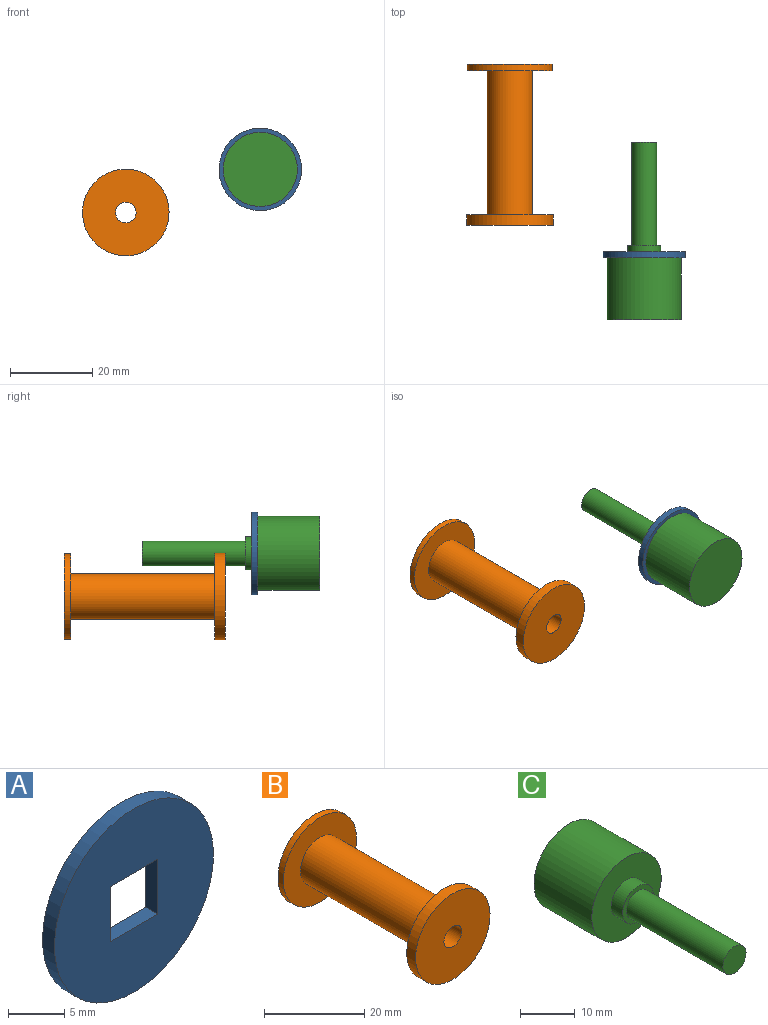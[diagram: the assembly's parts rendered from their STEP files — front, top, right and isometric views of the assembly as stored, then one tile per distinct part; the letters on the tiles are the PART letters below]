
ASSEMBLY  parts=3 mates=1
PART A: 7 faces, bbox 20x1.5x20 mm
  f0: plane 6x1.5mm, normal (0,0,-1), area 9mm2, adj f1,f4,f5,f6
  f1: plane 6x1.5mm, normal (-1,0,0), area 9mm2, adj f0,f2,f5,f6
  f2: plane 6x1.5mm, normal (0,0,1), area 9mm2, adj f1,f4,f5,f6
  f3: cylinder r=10mm len=20mm, axis (0,1,0), area 94.2mm2, adj f5,f6
  f4: plane 6x1.5mm, normal (1,0,0), area 9mm2, adj f0,f2,f5,f6
  f5: plane 20x20mm, normal (0,-1,0), area 278.2mm2, adj f0,f1,f2,f3,f4
  f6: plane 20x20mm, normal (0,1,0), area 278.2mm2, adj f0,f1,f2,f3,f4
PART B: 8 faces, bbox 21x39x21 mm
  f0: cylinder r=10.35mm len=20.7mm, axis (0,1,0), area 97.5mm2, adj f1,f2
  f1: plane 20.7x20.7mm, normal (0,-1,0), area 241.5mm2, adj f0,f3
  f2: plane 20.7x20.7mm, normal (0,1,0), area 316.9mm2, adj f0,f7
  f3: cylinder r=5.5mm len=35mm, axis (0,1,0), area 1209.5mm2, adj f1,f6
  f4: cylinder r=10.5mm len=21mm, axis (0,1,0), area 164.9mm2, adj f5,f6
  f5: plane 21x21mm, normal (0,-1,0), area 326.7mm2, adj f4,f7
  f6: plane 21x21mm, normal (0,1,0), area 251.3mm2, adj f3,f4
  f7: cylinder r=2.5mm len=39mm, axis (0,-1,0), area 612.6mm2, adj f2,f5
PART C: 7 faces, bbox 18x43x18 mm
  f0: cylinder r=9mm len=18mm, axis (0,1,0), area 848.2mm2, adj f1,f2
  f1: plane 18x18mm, normal (0,-1,0), area 204.2mm2, adj f0,f3
  f2: plane 18x18mm, normal (0,1,0), area 254.5mm2, adj f0
  f3: cylinder r=4mm len=8mm, axis (0,1,0), area 75.4mm2, adj f1,f4
  f4: plane 8x8mm, normal (0,-1,0), area 22mm2, adj f3,f5
  f5: cylinder r=3mm len=25mm, axis (0,1,0), area 471.2mm2, adj f4,f6
  f6: plane 6x6mm, normal (0,-1,0), area 28.3mm2, adj f5
PLACE A t=(8.37,-49.58,-4.04)mm
PLACE B t=(-24.25,-4.16,-14.5)mm
PLACE C rot(axis=(1,0,0),180deg) t=(8.37,-66.08,-4.04)mm
MATE fastened C.f3 <-> A.f3  axis (0,1,0) through (8.37,-51.08,-4.04)mm
